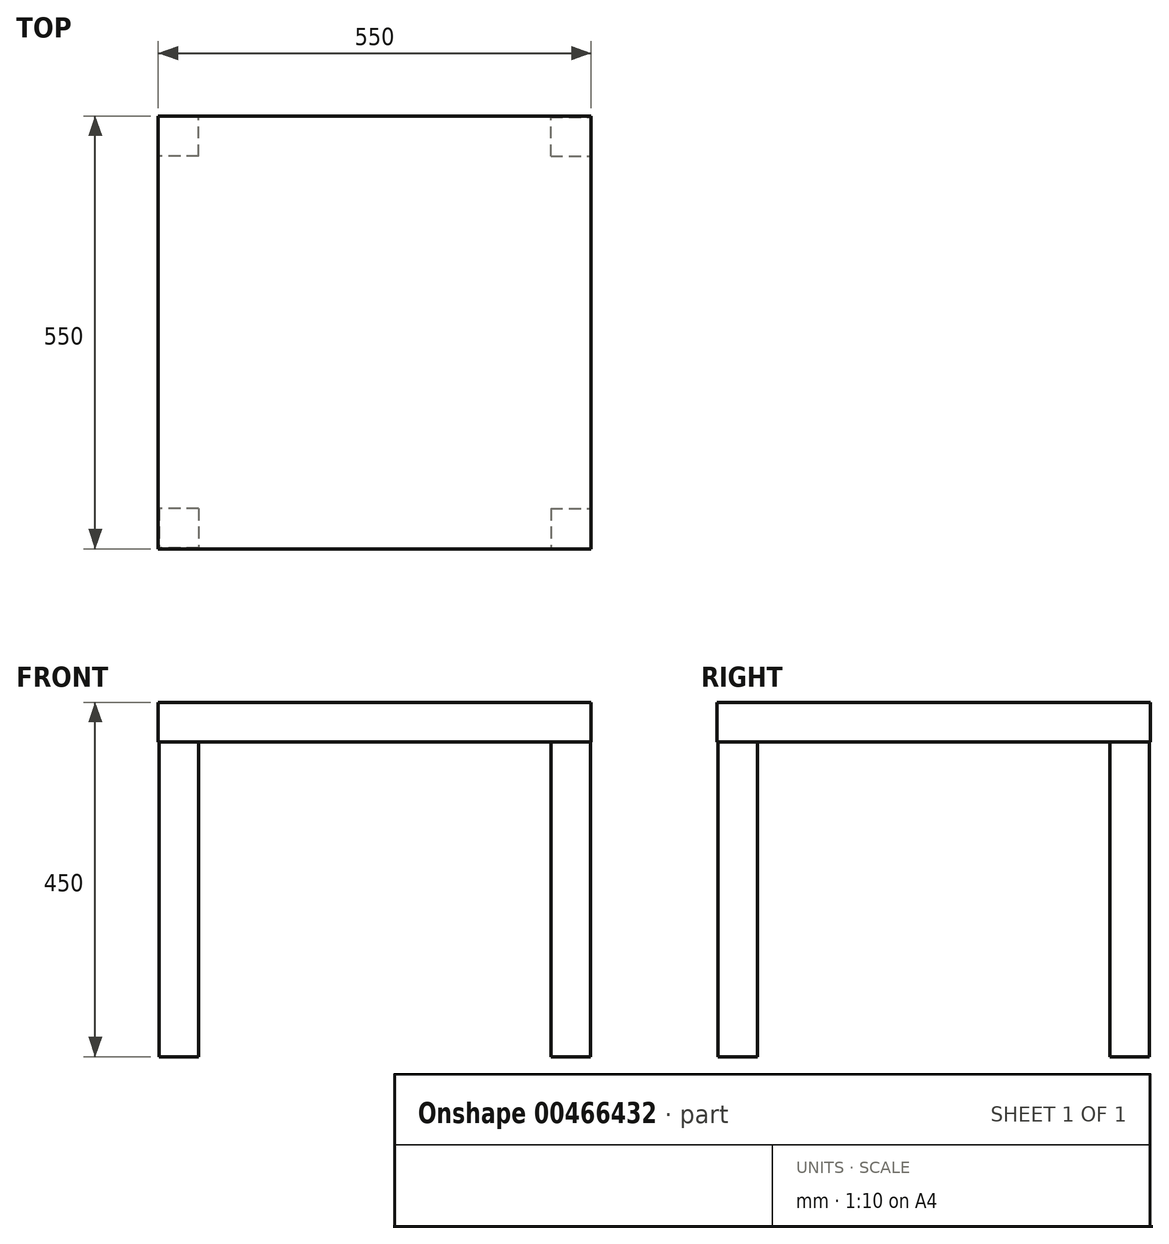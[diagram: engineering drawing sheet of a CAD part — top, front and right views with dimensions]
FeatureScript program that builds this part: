
annotation { "Feature Type Name" : "Feature", "Feature Type Description" : "" }
export const myFeature = defineFeature(function(context is Context, id is Id, definition is map)
    precondition{}
    {
        {
            var Q0;
            Q0=qCreatedBy(makeId("Top.planeOp"),FACE);
            var sketch = newSketch(context, id + "F0", { "sketchPlane" : qUnion([Q0])});
            skLineSegment(sketch, "E0.bottom", {"start": v(275, 275) * mm, "end": v(-275, 275) * mm});
            skLineSegment(sketch, "E0.top", {"start": v(275, -275) * mm, "end": v(-275, -275) * mm});
            skLineSegment(sketch, "E0.left", {"start": v(275, 275) * mm, "end": v(275, -275) * mm});
            skLineSegment(sketch, "E0.right", {"start": v(-275, 275) * mm, "end": v(-275, -275) * mm});
            skPoint(sketch, "E0.middle", {"position": v(0, 0) * mm});
            skSolve(sketch);
        }
        {
            var Q0;
            Q0 = qSketchRegion(id + "F0", true);
            extrude(context, id + "F1", {"entities" : qUnion([Q0]), "depth" : 50 * mm, "offsetDistance" : 25 * mm});
        }
        {
            var Q0;
            Q0=makeQuery(id+"F1.opExtrude","CAP_FACE",FACE,{"disambiguationData":[OSD([sQuery(id+"F0.wireOp",EDGE,"E0.bottom"),sQuery(id+"F0.wireOp",EDGE,"E0.top"),sQuery(id+"F0.wireOp",EDGE,"E0.left"),sQuery(id+"F0.wireOp",EDGE,"E0.right")])],"isStart":true});
            var sketch = newSketch(context, id + "F2", { "sketchPlane" : qUnion([Q0])});
            skLineSegment(sketch, "E1.bottom", {"start": v(-223.8, 223.8) * mm, "end": v(-273.8, 223.8) * mm});
            skLineSegment(sketch, "E1.top", {"start": v(-223.8, 273.8) * mm, "end": v(-273.8, 273.8) * mm});
            skLineSegment(sketch, "E1.left", {"start": v(-223.8, 223.8) * mm, "end": v(-223.8, 273.8) * mm});
            skLineSegment(sketch, "E1.right", {"start": v(-273.8, 223.8) * mm, "end": v(-273.8, 273.8) * mm});
            skLineSegment(sketch, "E2.MirrorCS", {"start": v(273.8, 223.8) * mm, "end": v(273.8, 273.8) * mm});
            skLineSegment(sketch, "E3.MirrorCS", {"start": v(223.8, 223.8) * mm, "end": v(223.8, 273.8) * mm});
            skLineSegment(sketch, "E4.MirrorCS", {"start": v(223.8, 273.8) * mm, "end": v(273.8, 273.8) * mm});
            skLineSegment(sketch, "E5.MirrorCS", {"start": v(223.8, 223.8) * mm, "end": v(273.8, 223.8) * mm});
            skLineSegment(sketch, "E6.MirrorCS", {"start": v(-223.8, -273.8) * mm, "end": v(-273.8, -273.8) * mm});
            skLineSegment(sketch, "E7.MirrorCS", {"start": v(-223.8, -223.8) * mm, "end": v(-273.8, -223.8) * mm});
            skLineSegment(sketch, "E8.MirrorCS", {"start": v(-223.8, -223.8) * mm, "end": v(-223.8, -273.8) * mm});
            skLineSegment(sketch, "E9.MirrorCS", {"start": v(-273.8, -223.8) * mm, "end": v(-273.8, -273.8) * mm});
            skLineSegment(sketch, "E10.MirrorCS", {"start": v(273.8, -223.8) * mm, "end": v(273.8, -273.8) * mm});
            skLineSegment(sketch, "E11.MirrorCS", {"start": v(223.8, -223.8) * mm, "end": v(223.8, -273.8) * mm});
            skLineSegment(sketch, "E12.MirrorCS", {"start": v(223.8, -223.8) * mm, "end": v(273.8, -223.8) * mm});
            skLineSegment(sketch, "E13.MirrorCS", {"start": v(223.8, -273.8) * mm, "end": v(273.8, -273.8) * mm});
            skSolve(sketch);
        }
        {
            var Q0;
            Q0=makeQuery(id+"F2.imprint","IMPRINT",FACE,{"disambiguationData":[TD([[makeQuery(id+"F2.imprint","IMPRINT",EDGE,{"derivedFrom":sQuery(id+"F2.wireOp",EDGE,"E1.bottom")}),-1.0]])]});
            var Q1;
            Q1=makeQuery(id+"F2.imprint","IMPRINT",FACE,{"disambiguationData":[TD([[makeQuery(id+"F2.imprint","IMPRINT",EDGE,{"derivedFrom":sQuery(id+"F2.wireOp",EDGE,"E2.MirrorCS")}),1.0]])]});
            var Q2;
            Q2=makeQuery(id+"F2.imprint","IMPRINT",FACE,{"disambiguationData":[TD([[makeQuery(id+"F2.imprint","IMPRINT",EDGE,{"derivedFrom":sQuery(id+"F2.wireOp",EDGE,"E10.MirrorCS")}),-1.0]])]});
            var Q3;
            Q3=makeQuery(id+"F2.imprint","IMPRINT",FACE,{"disambiguationData":[TD([[makeQuery(id+"F2.imprint","IMPRINT",EDGE,{"derivedFrom":sQuery(id+"F2.wireOp",EDGE,"E6.MirrorCS")}),-1.0]])]});
            extrude(context, id + "F3", {"entities" : qUnion([Q0, Q1, Q2, Q3]), "operationType" : NewBodyOperationType.ADD, "depth" : 400 * mm, "offsetDistance" : 25 * mm});
        }
    });
